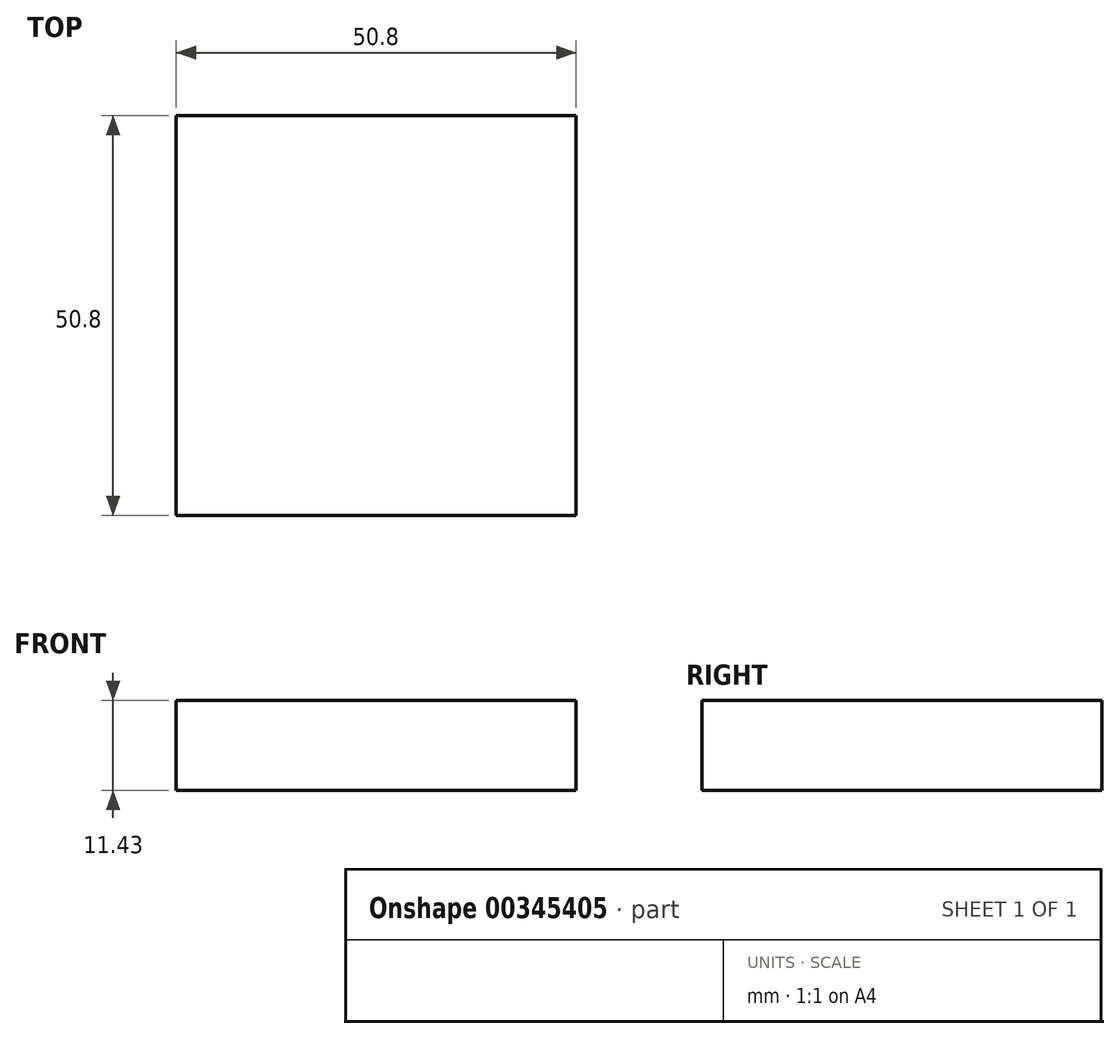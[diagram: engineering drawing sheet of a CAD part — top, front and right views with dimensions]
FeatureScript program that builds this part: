
annotation { "Feature Type Name" : "Feature", "Feature Type Description" : "" }
export const myFeature = defineFeature(function(context is Context, id is Id, definition is map)
    precondition{}
    {
        {
            var Q0;
            Q0=qCreatedBy(makeId("Top.planeOp"),FACE);
            var sketch = newSketch(context, id + "F0", { "sketchPlane" : qUnion([Q0])});
            skLineSegment(sketch, "E0.bottom", {"start": v(0, 0) * mm, "end": v(50.8, 0) * mm});
            skLineSegment(sketch, "E0.top", {"start": v(0, 50.8) * mm, "end": v(50.8, 50.8) * mm});
            skLineSegment(sketch, "E0.left", {"start": v(0, 0) * mm, "end": v(0, 50.8) * mm});
            skLineSegment(sketch, "E0.right", {"start": v(50.8, 0) * mm, "end": v(50.8, 50.8) * mm});
            skSolve(sketch);
        }
        {
            var Q0;
            Q0 = qSketchRegion(id + "F0", true);
            extrude(context, id + "F1", {"entities" : qUnion([Q0]), "depth" : 11.43 * mm});
        }
    });
